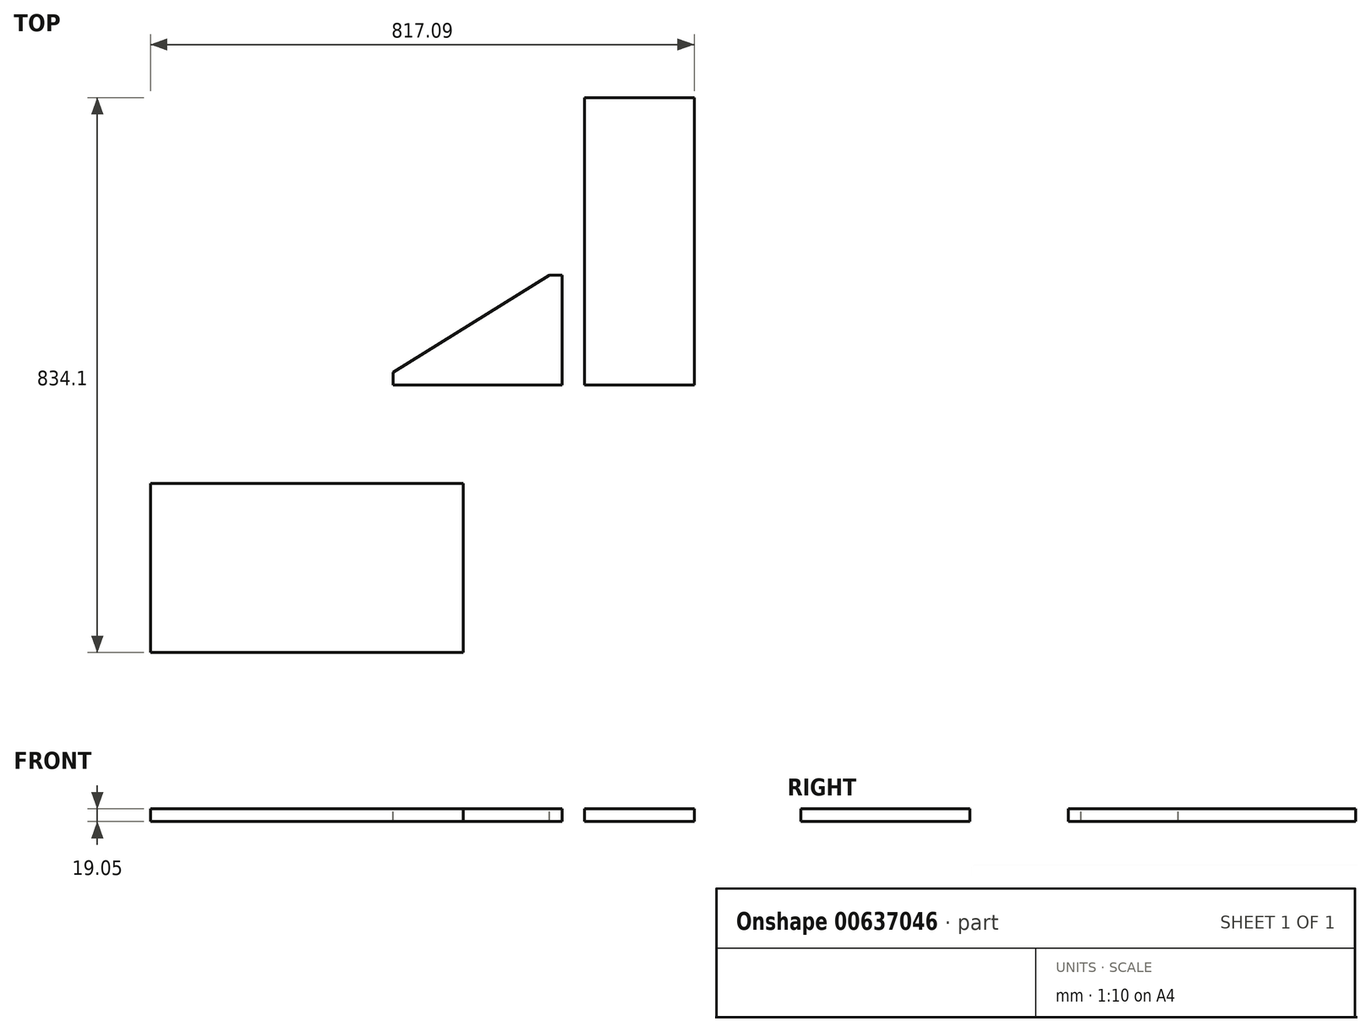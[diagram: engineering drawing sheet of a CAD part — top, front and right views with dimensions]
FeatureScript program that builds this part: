
annotation { "Feature Type Name" : "Feature", "Feature Type Description" : "" }
export const myFeature = defineFeature(function(context is Context, id is Id, definition is map)
    precondition{}
    {
        {
            var Q0;
            Q0=qCreatedBy(makeId("Top.planeOp"),FACE);
            var sketch = newSketch(context, id + "F0", { "sketchPlane" : qUnion([Q0])});
            skLineSegment(sketch, "E0.bottom", {"start": v(0, 0) * mm, "end": v(165.1, 0) * mm});
            skLineSegment(sketch, "E0.top", {"start": v(0, 431.8) * mm, "end": v(165.1, 431.8) * mm});
            skLineSegment(sketch, "E0.left", {"start": v(0, 0) * mm, "end": v(0, 431.8) * mm});
            skLineSegment(sketch, "E0.right", {"start": v(165.1, 0) * mm, "end": v(165.1, 431.8) * mm});
            skSolve(sketch);
        }
        {
            var Q0;
            Q0 = qSketchRegion(id + "F0", true);
            extrude(context, id + "F1", {"entities" : qUnion([Q0]), "depth" : 19.05 * mm, "offsetDistance" : 25.4 * mm});
        }
        {
            var Q0;
            Q0=qCreatedBy(makeId("Top.planeOp"),FACE);
            var sketch = newSketch(context, id + "F2", { "sketchPlane" : qUnion([Q0])});
            skLineSegment(sketch, "E1.bottom", {"start": v(-287.31, 0) * mm, "end": v(-33.31, 0) * mm});
            skLineSegment(sketch, "E1.top", {"start": v(-287.31, 165.1) * mm, "end": v(-33.31, 165.1) * mm});
            skLineSegment(sketch, "E1.left", {"start": v(-287.31, 0) * mm, "end": v(-287.31, 165.1) * mm});
            skLineSegment(sketch, "E1.right", {"start": v(-33.31, 0) * mm, "end": v(-33.31, 165.1) * mm});
            skLineSegment(sketch, "E2", {"start": v(0, 0) * mm, "end": v(-33.31, 0) * mm});
            skSolve(sketch);
        }
        {
            var Q0;
            Q0 = qSketchRegion(id + "F2", true);
            extrude(context, id + "F3", {"entities" : qUnion([Q0]), "depth" : 19.05 * mm, "offsetDistance" : 25.4 * mm});
        }
        {
            var Q0;
            Q0=makeQuery(id+"F3.opExtrude","CAP_FACE",FACE,{"disambiguationData":[OSD([sQuery(id+"F2.wireOp",EDGE,"E1.bottom"),sQuery(id+"F2.wireOp",EDGE,"E1.top"),sQuery(id+"F2.wireOp",EDGE,"E1.left"),sQuery(id+"F2.wireOp",EDGE,"E1.right")])],"isStart":false});
            var sketch = newSketch(context, id + "F4", { "sketchPlane" : qUnion([Q0])});
            skLineSegment(sketch, "E3", {"start": v(-33.31, 165.1) * mm, "end": v(-52.36, 165.1) * mm});
            skLineSegment(sketch, "E4", {"start": v(-287.31, 0) * mm, "end": v(-287.31, 19.05) * mm});
            skLineSegment(sketch, "E5", {"start": v(-52.36, 165.1) * mm, "end": v(-287.31, 19.05) * mm});
            skSolve(sketch);
        }
        {
            var Q0;
            Q0 = qSketchRegion(id + "F4", true);
            var Q1;
            {var subQ0=sQuery(id+"F4.wireOp",EDGE,"E5");Q1=makeQuery(id+"F4.imprint","IMPRINT",FACE,{"disambiguationData":[TD([[makeQuery(id+"F4.imprint","IMPRINT",EDGE,{"derivedFrom":subQ0}),-1.0]])]});}
            extrude(context, id + "F5", {"entities" : qUnion([Q0, Q1]), "operationType" : NewBodyOperationType.REMOVE, "endBound" : BoundingType.THROUGH_ALL, "oppositeDirection" : true, "depth" : 25.4 * mm, "offsetDistance" : 25.4 * mm});
        }
        {
            var Q0;
            Q0=qCreatedBy(makeId("Top.planeOp"),FACE);
            var sketch = newSketch(context, id + "F6", { "sketchPlane" : qUnion([Q0])});
            skLineSegment(sketch, "E6.bottom", {"start": v(-652, -148.3) * mm, "end": v(-182.1, -148.3) * mm});
            skLineSegment(sketch, "E6.top", {"start": v(-652, -402.3) * mm, "end": v(-182.1, -402.3) * mm});
            skLineSegment(sketch, "E6.left", {"start": v(-652, -148.3) * mm, "end": v(-652, -402.3) * mm});
            skLineSegment(sketch, "E6.right", {"start": v(-182.1, -148.3) * mm, "end": v(-182.1, -402.3) * mm});
            skSolve(sketch);
        }
        {
            var Q0;
            Q0=makeQuery(id+"F6.imprint","IMPRINT",FACE,{"disambiguationData":[TD([[makeQuery(id+"F6.imprint","IMPRINT",EDGE,{"derivedFrom":sQuery(id+"F6.wireOp",EDGE,"E6.bottom")}),-1.0]])]});
            extrude(context, id + "F7", {"entities" : qUnion([Q0]), "depth" : 19.05 * mm, "offsetDistance" : 25.4 * mm});
        }
    });
